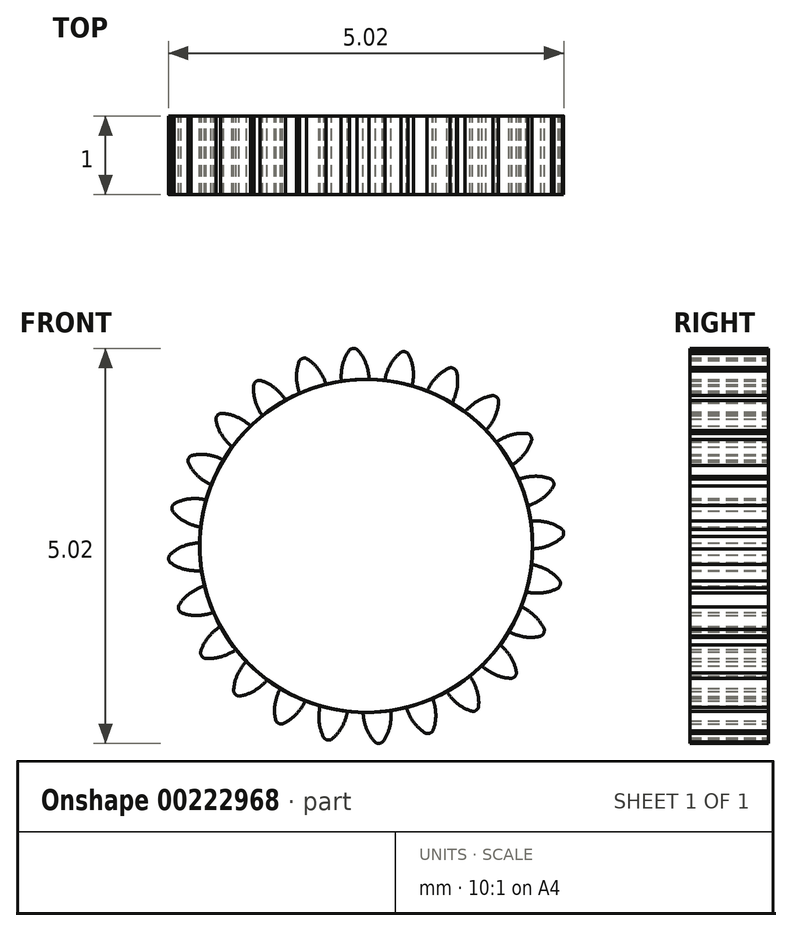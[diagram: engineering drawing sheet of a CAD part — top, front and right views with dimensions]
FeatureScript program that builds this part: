
annotation { "Feature Type Name" : "Feature", "Feature Type Description" : "" }
export const myFeature = defineFeature(function(context is Context, id is Id, definition is map)
    precondition{}
    {
        {
            var Q0;
            Q0=qCreatedBy(makeId("Front.planeOp"),FACE);
            var sketch = newSketch(context, id + "F0", { "sketchPlane" : qUnion([Q0])});
            skCircle(sketch, "E0", {"center": v(0, 0) * mm, "radius": 2.12 * mm});
            skCircle(sketch, "E1", {"center": v(0, 0) * mm, "radius": 2.31 * mm, "construction": true});
            skCircle(sketch, "E2", {"center": v(0, 0) * mm, "radius": 2.5 * mm, "construction": true});
            skLineSegment(sketch, "E3", {"start": v(0, 0) * mm, "end": v(0, 4.32) * mm, "construction": true});
            skLineSegment(sketch, "E4", {"start": v(0, 0) * mm, "end": v(-0.28, 4.27) * mm, "construction": true});
            skLineSegment(sketch, "E5", {"start": v(0, 2.31) * mm, "end": v(-3.6, 2.31) * mm, "construction": true});
            skLineSegment(sketch, "E6", {"start": v(0, 2.31) * mm, "end": v(-3.77, 0.94) * mm});
            skCircle(sketch, "E7", {"center": v(0, 2.31) * mm, "radius": 0.57 * mm, "construction": true});
            skCircle(sketch, "E8", {"center": v(0, 0) * mm, "radius": 2.17 * mm, "construction": true});
            skCircle(sketch, "E9", {"center": v(-0.54, 2.1) * mm, "radius": 0.57 * mm, "construction": true});
            skArc(sketch, "E10", {"start": v(0, 2.31) * mm, "mid": v(-0.05, 2.4) * mm, "end": v(-0.12, 2.5) * mm});
            skArc(sketch, "E11", {"start": v(0.04, 2.11) * mm, "mid": v(0.03, 2.21) * mm, "end": v(0, 2.31) * mm});
            skArc(sketch, "E12.MirrorCS", {"start": v(-0.31, 2.1) * mm, "mid": v(-0.32, 2.2) * mm, "end": v(-0.3, 2.3) * mm});
            skArc(sketch, "E13.MirrorCS", {"start": v(-0.3, 2.3) * mm, "mid": v(-0.27, 2.4) * mm, "end": v(-0.2, 2.5) * mm});
            skArc(sketch, "E14", {"start": v(-0.12, 2.5) * mm, "mid": v(-0.16, 2.5) * mm, "end": v(-0.2, 2.5) * mm});
            skSolve(sketch);
        }
        {
            var Q0;
            {var subQ0=sQuery(id+"F0.wireOp",EDGE,"E0");var subQ1=makeQuery(id+"F0.imprint","INTERSECT",VERTEX,{"derivedFrom":[subQ0,sQuery(id+"F0.wireOp",EDGE,"E11")]});Q0=makeQuery(id+"F0.imprint","IMPRINT",FACE,{"disambiguationData":[TD([[makeQuery(id+"F0.imprint","IMPRINT",EDGE,{"disambiguationData":[TD([[subQ1,-1.0]])],"derivedFrom":subQ0}),1.0]])]});}
            var Q1;
            {var subQ0=sQuery(id+"F0.wireOp",EDGE,"E11");Q1=makeQuery(id+"F0.imprint","IMPRINT",FACE,{"disambiguationData":[TD([[makeQuery(id+"F0.imprint","IMPRINT",EDGE,{"derivedFrom":subQ0}),1.0]])]});}
            var Q2;
            {var subQ4=sQuery(id+"F0.wireOp",EDGE,"E10");Q2=makeQuery(id+"F0.imprint","IMPRINT",FACE,{"disambiguationData":[TD([[makeQuery(id+"F0.imprint","IMPRINT",EDGE,{"derivedFrom":subQ4}),1.0]])]});}
            extrude(context, id + "F1", {"entities" : qUnion([Q0, Q1, Q2]), "depth" : 1 * mm});
        }
        {
            var Q0;
            Q0=makeQuery(id+"F1.opExtrude","SWEPT_BODY",BODY,{"disambiguationData":[OSD([sQuery(id+"F0.wireOp",EDGE,"E0"),sQuery(id+"F0.wireOp",EDGE,"E10"),sQuery(id+"F0.wireOp",EDGE,"E11"),sQuery(id+"F0.wireOp",EDGE,"E12.MirrorCS"),sQuery(id+"F0.wireOp",EDGE,"E13.MirrorCS"),sQuery(id+"F0.wireOp",EDGE,"E14")])]});
            var Q1;
            Q1=makeQuery(id+"F1.opExtrude","SWEPT_FACE",FACE,{"disambiguationData":[OSD([sQuery(id+"F0.wireOp",EDGE,"E0")])]});
            circularPattern(context, id + "F2", {"entities" : qUnion([Q0]), "axis" : qUnion([Q1]), "angle" : 15 * degree, "instanceCount" : 24});
        }
    });
